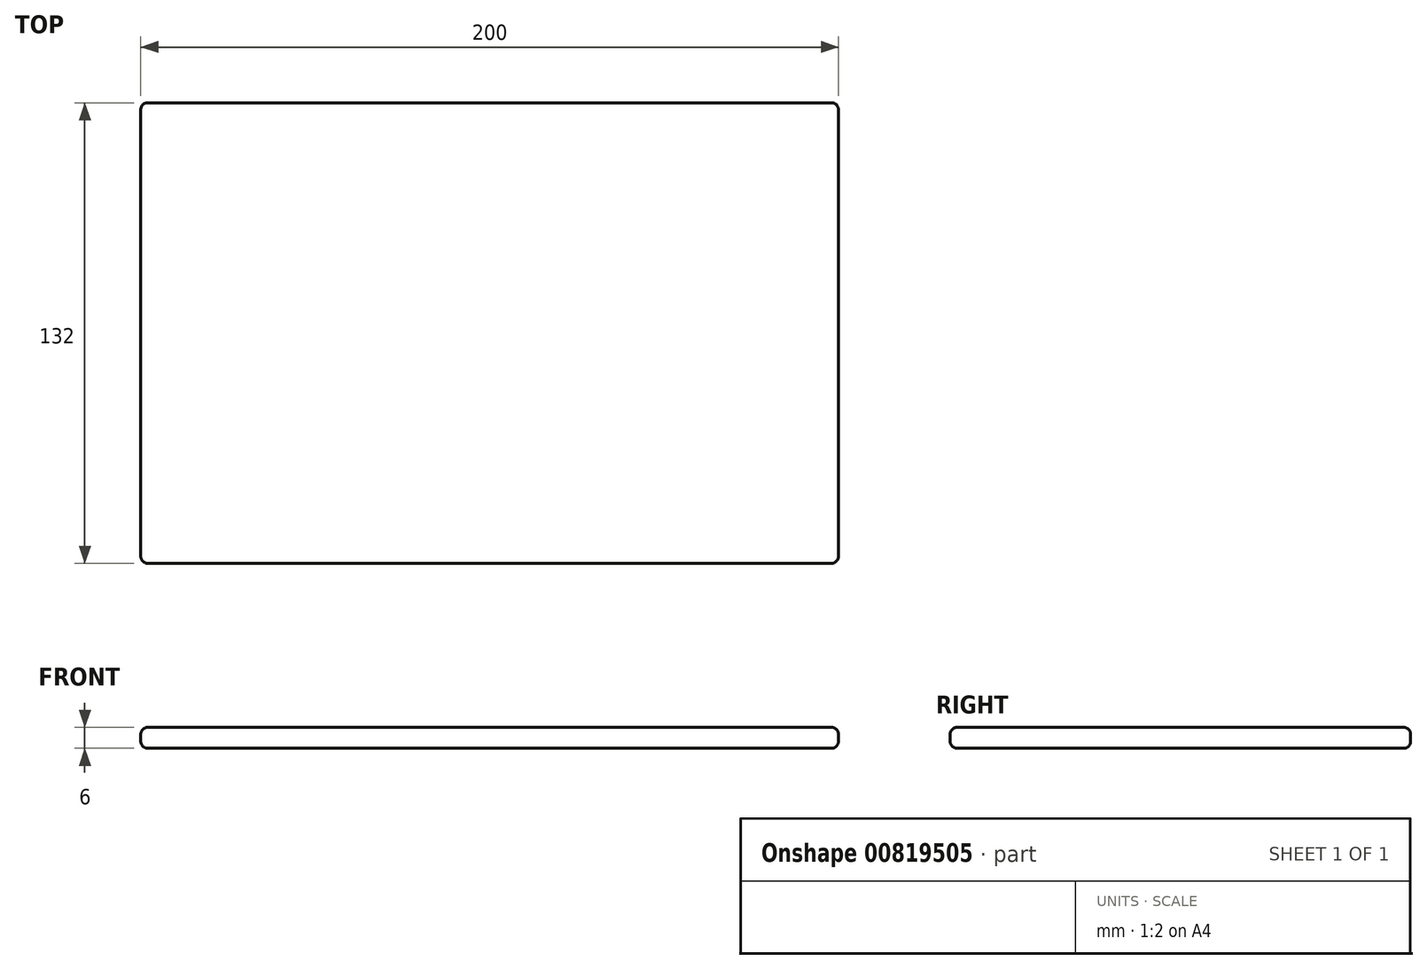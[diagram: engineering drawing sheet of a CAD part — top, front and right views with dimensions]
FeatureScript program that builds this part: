
annotation { "Feature Type Name" : "Feature", "Feature Type Description" : "" }
export const myFeature = defineFeature(function(context is Context, id is Id, definition is map)
    precondition{}
    {
        {
            var Q0;
            Q0=qCreatedBy(makeId("Top.planeOp"),FACE);
            var sketch = newSketch(context, id + "F0", { "sketchPlane" : qUnion([Q0])});
            skLineSegment(sketch, "E0.bottom", {"start": v(100, 66) * mm, "end": v(-100, 66) * mm});
            skLineSegment(sketch, "E0.top", {"start": v(100, -66) * mm, "end": v(-100, -66) * mm});
            skLineSegment(sketch, "E0.left", {"start": v(100, 66) * mm, "end": v(100, -66) * mm});
            skLineSegment(sketch, "E0.right", {"start": v(-100, 66) * mm, "end": v(-100, -66) * mm});
            skPoint(sketch, "E0.middle", {"position": v(0, 0) * mm});
            skSolve(sketch);
        }
        {
            var Q0;
            Q0=makeQuery(id+"F0.imprint","IMPRINT",FACE,{"disambiguationData":[TD([[makeQuery(id+"F0.imprint","IMPRINT",EDGE,{"derivedFrom":sQuery(id+"F0.wireOp",EDGE,"E0.bottom")}),1.0]])]});
            var sketch = newSketch(context, id + "F1", { "sketchPlane" : qUnion([Q0])});
            skSolve(sketch);
        }
        {
            var Q0;
            Q0 = qSketchRegion(id + "F1", true);
            var Q1;
            Q1=makeQuery(id+"F1.imprint","IMPRINT",FACE,{"disambiguationData":[TD([[makeQuery(id+"F1.imprint","IMPRINT",EDGE,{"derivedFrom":makeQuery(id+"F0.imprint","IMPRINT",EDGE,{"derivedFrom":sQuery(id+"F0.wireOp",EDGE,"E0.bottom")})}),1.0]])]});
            extrude(context, id + "F2", {"entities" : qUnion([Q0, Q1]), "depth" : 6 * mm, "offsetDistance" : 25 * mm});
        }
        {
            var Q0;
            Q0=makeQuery(id+"F2.opExtrude","CAP_FACE",FACE,{"disambiguationData":[OSD([sQuery(id+"F0.wireOp",EDGE,"E0.bottom"),sQuery(id+"F0.wireOp",EDGE,"E0.top"),sQuery(id+"F0.wireOp",EDGE,"E0.left"),sQuery(id+"F0.wireOp",EDGE,"E0.right")])],"isStart":false});
            var Q1;
            Q1=makeQuery(id+"F2.opExtrude","SWEPT_EDGE",EDGE,{"disambiguationData":[OSD([sQuery(id+"F0.wireOp",EDGE,"E0.top"),sQuery(id+"F0.wireOp",EDGE,"E0.right")])]});
            var Q2;
            Q2=makeQuery(id+"F2.opExtrude","CAP_FACE",FACE,{"disambiguationData":[OSD([sQuery(id+"F0.wireOp",EDGE,"E0.bottom"),sQuery(id+"F0.wireOp",EDGE,"E0.top"),sQuery(id+"F0.wireOp",EDGE,"E0.left"),sQuery(id+"F0.wireOp",EDGE,"E0.right")])],"isStart":true});
            var Q3;
            Q3=makeQuery(id+"F2.opExtrude","SWEPT_EDGE",EDGE,{"disambiguationData":[OSD([sQuery(id+"F0.wireOp",EDGE,"E0.top"),sQuery(id+"F0.wireOp",EDGE,"E0.left")])]});
            var Q4;
            Q4=makeQuery(id+"F2.opExtrude","SWEPT_EDGE",EDGE,{"disambiguationData":[OSD([sQuery(id+"F0.wireOp",EDGE,"E0.bottom"),sQuery(id+"F0.wireOp",EDGE,"E0.left")])]});
            var Q5;
            Q5=makeQuery(id+"F2.opExtrude","SWEPT_EDGE",EDGE,{"disambiguationData":[OSD([sQuery(id+"F0.wireOp",EDGE,"E0.bottom"),sQuery(id+"F0.wireOp",EDGE,"E0.right")])]});
            fillet(context, id + "F3", {"entities" : qUnion([Q0, Q1, Q2, Q3, Q4, Q5]), "radius" : 2 * mm, "tangentPropagation" : true, "allowEdgeOverflow" : false});
        }
    });
